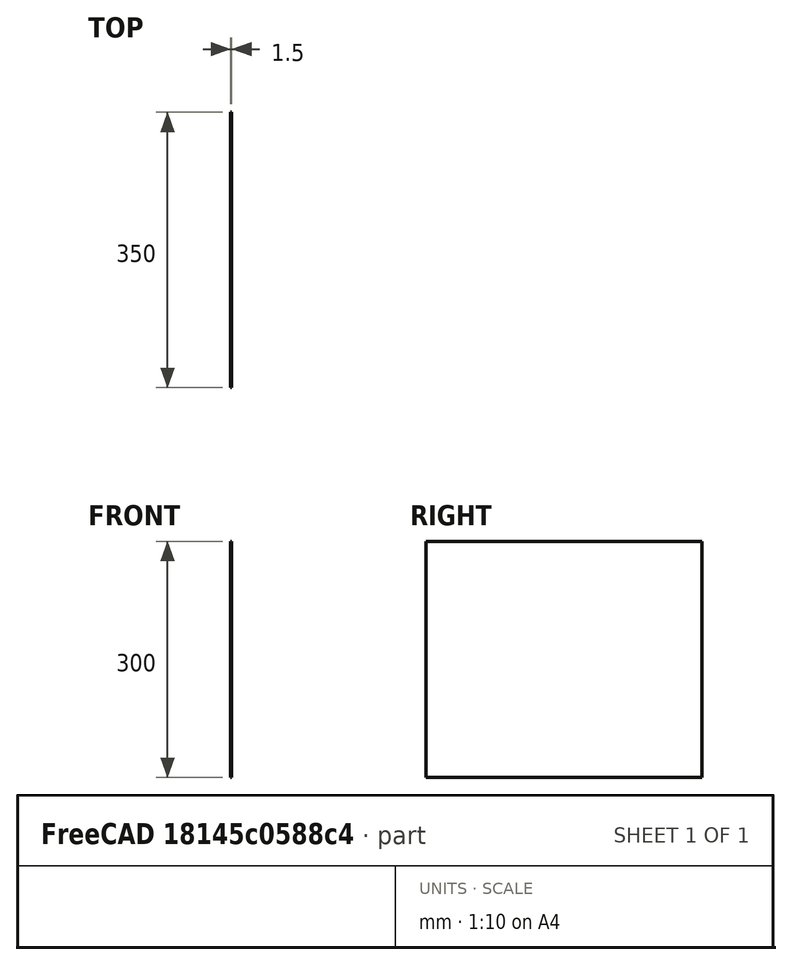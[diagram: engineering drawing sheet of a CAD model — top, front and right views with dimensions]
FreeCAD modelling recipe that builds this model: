
FCSTD DOCUMENT  (FreeCAD 2022.1112R26244 +5306 (Git))
Label: Tailbox Bulkhead
License: All rights reserved
LicenseURL: http://en.wikipedia.org/wiki/All_rights_reserved
objects: Sketcher::SketchObject×1, PartDesign::Pad×1, PartDesign::Body×1
note: 6 computed .brp shape members not serialized (recipe doc carries the construction recipe); baked Part::Feature solids carry a one-line shape summary decoded from their .brp
EXTERNAL_REF file=Tailbox.FCStd obj=Spreadsheet

FEATURE [Sketcher::SketchObject] Sketch
  ArcFitTolerance = 0
  AttachmentSupport = -> [YZ_Plane]
  ExternalBSplineMaxDegree = 0
  ExternalBSplineTolerance = 0
  FullyConstrained = true
  InternalTolerance = 1e-06
  MakeInternals = false
  MapMode = 5
  Placement = pos=(0,0,0) rot=(0.57735,0.57735,0.57735;2.0944rad)
  Support = -> [YZ_Plane]
  TreeRank = 0
  expr: Constraints[6] = Tailbox#<<dims>>.z_up
  expr: Constraints[7] = Tailbox#<<dims>>.y_max
  sketch-geometry (4):
    g0: LineSegment StartX=-175 StartY=0 StartZ=0 EndX=-175 EndY=300 EndZ=0
    g1: LineSegment StartX=-175 StartY=300 StartZ=0 EndX=175 EndY=300 EndZ=0
    g2: LineSegment StartX=175 StartY=300 StartZ=0 EndX=175 EndY=0 EndZ=0
    g3: LineSegment StartX=175 StartY=0 StartZ=0 EndX=-175 EndY=0 EndZ=0
  constraints (11):
    c: Vertical(g0)
    c: Coincident(g0,g1)
    c: Coincident(g1,g2)
    c: Vertical(g2)
    c: PointOnObject(g3,g-1)
    c: PointOnObject(g3,g-1)
    c: DistanceY(g1) = 300
    c: DistanceX(g1,g1) = 350
    c: Coincident(g2,g3)
    c: Coincident(g0,g3)
    c: Symmetric(g0,g1,g-2)
FEATURE [PartDesign::Pad] Pad
  AddSubType = 0
  AlongSketchNormal = false
  AutoTaperInnerAngle = false
  CheckUpToFaceLimits = true
  ClaimChildren = false
  Direction = (1,-2e-16,3e-16)
  Fit = 0
  FitJoin = 0
  InnerFit = 0
  InnerFitJoin = 0
  Length = 1.5
  Length2 = 100
  NewSolid = false
  Profile = -> Sketch
  ReferenceAxis = -> Sketch [N_Axis]
  Suppress = false
  TaperInnerAngle = 0
  TaperInnerAngleRev = 0
  TreeRank = 0
  Type = 0
  _ProfileBasedVersion = 0
  expr: Length = Tailbox#<<dims>>.panel_thickness
FEATURE [PartDesign::Body] Body  label="Bulkhead"
  AutoGroupSolids = false
  ClaimAllChildren = false
  ExportMode = 0
  Group = -> [Sketch,Pad]
  Origin = -> Origin
  Tip = -> Pad
  TreeRank = 0
  _ExportChildren = -> [Pad]
  _GroupVersion = 1
